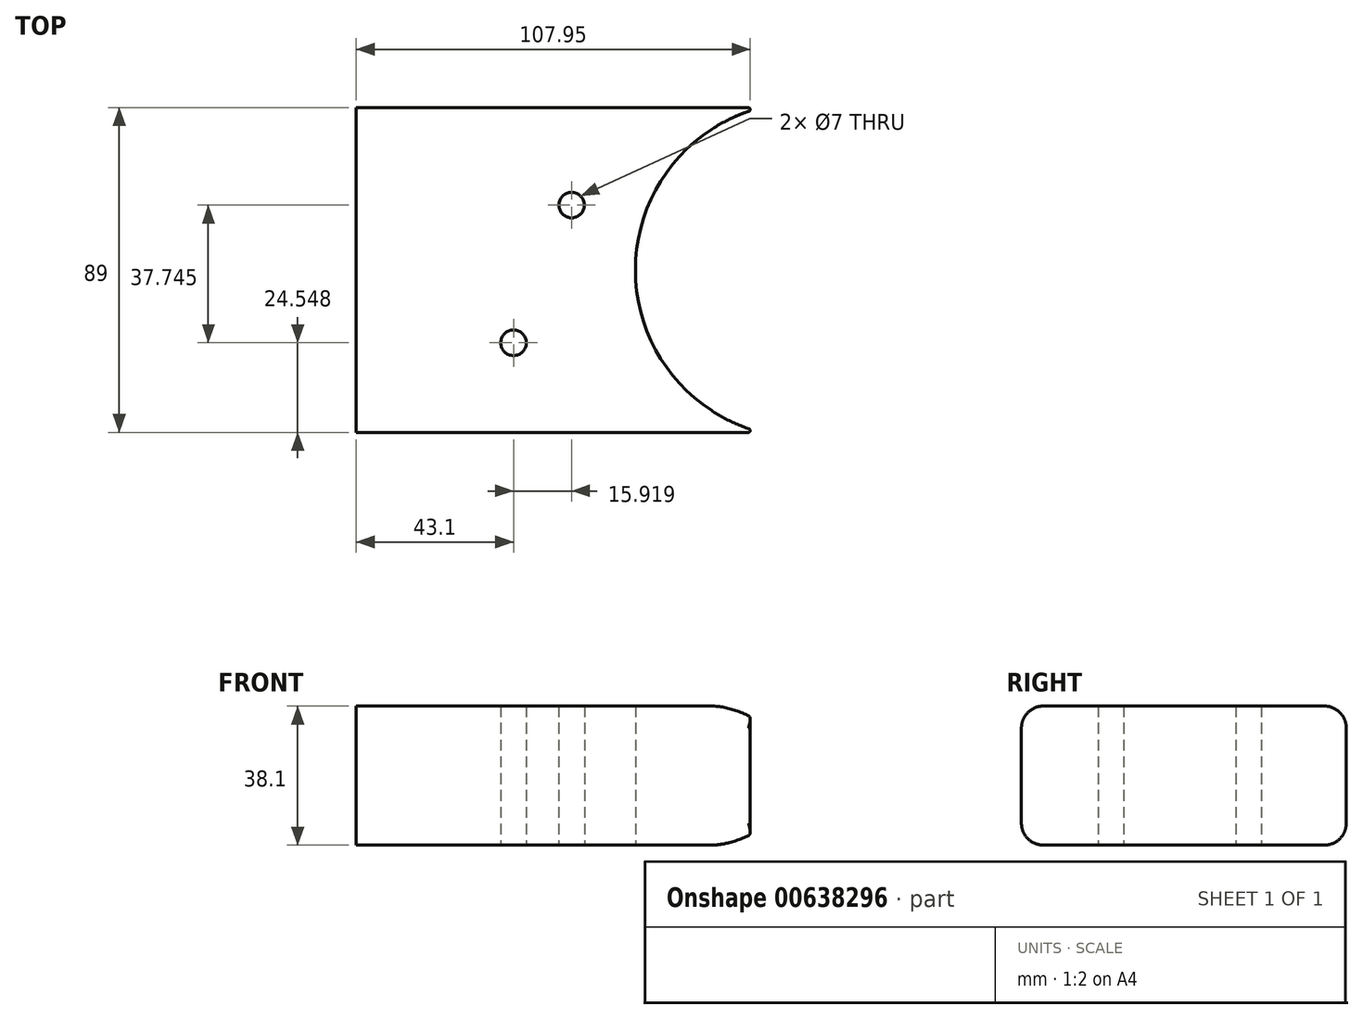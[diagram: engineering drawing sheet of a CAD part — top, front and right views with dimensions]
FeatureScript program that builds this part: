
annotation { "Feature Type Name" : "Feature", "Feature Type Description" : "" }
export const myFeature = defineFeature(function(context is Context, id is Id, definition is map)
    precondition{}
    {
        {
            var Q0;
            Q0=qCreatedBy(makeId("Top.planeOp"),FACE);
            var sketch = newSketch(context, id + "F0", { "sketchPlane" : qUnion([Q0])});
            skLineSegment(sketch, "E0.bottom", {"start": v(-56, 44.5) * mm, "end": v(56, 44.5) * mm});
            skLineSegment(sketch, "E0.top", {"start": v(-56, -44.5) * mm, "end": v(56, -44.5) * mm});
            skLineSegment(sketch, "E0.left", {"start": v(-56, 44.5) * mm, "end": v(-56, -44.5) * mm});
            skLineSegment(sketch, "E0.right", {"start": v(56, 44.5) * mm, "end": v(56, -44.5) * mm});
            skPoint(sketch, "E0.middle", {"position": v(0, 0) * mm});
            skCircle(sketch, "E1", {"center": v(66.5, 0) * mm, "radius": 46 * mm});
            skCircle(sketch, "E2", {"center": v(3.02, 17.8) * mm, "radius": 3.5 * mm});
            skCircle(sketch, "E3", {"center": v(-12.9, -19.95) * mm, "radius": 3.5 * mm});
            skSolve(sketch);
        }
        {
            var Q0;
            {var subQ5=sQuery(id+"F0.wireOp",EDGE,"E0.left");Q0=makeQuery(id+"F0.imprint","IMPRINT",FACE,{"disambiguationData":[TD([[makeQuery(id+"F0.imprint","IMPRINT",EDGE,{"derivedFrom":subQ5}),1.0]])]});}
            extrude(context, id + "F1", {"entities" : qUnion([Q0]), "endBound" : BoundingType.SYMMETRIC, "depth" : 38.1 * mm, "offsetDistance" : 25 * mm});
        }
        {
            var Q0;
            Q0=makeQuery(id+"F1.opExtrude","SWEPT_EDGE",EDGE,{"disambiguationData":[OSD([sQuery(id+"F0.wireOp",EDGE,"E0.bottom"),sQuery(id+"F0.wireOp",EDGE,"E1")])]});
            var Q1;
            Q1=makeQuery(id+"F1.opExtrude","SWEPT_EDGE",EDGE,{"disambiguationData":[OSD([sQuery(id+"F0.wireOp",EDGE,"E0.top"),sQuery(id+"F0.wireOp",EDGE,"E1")])]});
            fillet(context, id + "F2", {"entities" : qUnion([Q0, Q1]), "radius" : .5 * mm, "tangentPropagation" : true, "allowEdgeOverflow" : false});
        }
        {
            var Q0;
            Q0=makeQuery(id+"F1.opExtrude","CAP_EDGE",EDGE,{"disambiguationData":[OSD([sQuery(id+"F0.wireOp",EDGE,"E0.top")])],"isStart":false});
            var Q1;
            Q1=makeQuery(id+"F1.opExtrude","CAP_EDGE",EDGE,{"disambiguationData":[OSD([sQuery(id+"F0.wireOp",EDGE,"E0.top")])],"isStart":true});
            var Q2;
            Q2=makeQuery(id+"F1.opExtrude","CAP_EDGE",EDGE,{"disambiguationData":[OSD([sQuery(id+"F0.wireOp",EDGE,"E0.bottom")])],"isStart":false});
            var Q3;
            Q3=makeQuery(id+"F1.opExtrude","CAP_EDGE",EDGE,{"disambiguationData":[OSD([sQuery(id+"F0.wireOp",EDGE,"E0.bottom")])],"isStart":true});
            fillet(context, id + "F3", {"entities" : qUnion([Q0, Q1, Q2, Q3]), "radius" : 6 * mm, "allowEdgeOverflow" : false});
        }
    });
